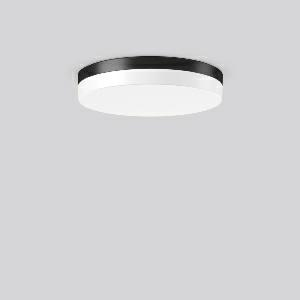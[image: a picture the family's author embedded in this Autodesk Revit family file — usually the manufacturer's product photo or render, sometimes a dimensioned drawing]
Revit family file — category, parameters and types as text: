
# Revit family: flat_slim_round_312632_0031_76_b1a7
name_source: partatom
category: Lighting Fixtures
units: mm (PartAtom-declared; Revit-internal decimal feet)

## family parameters
Cut with Voids When Loaded = No
Host = Face
Light Source = No
Part Type = Normal
Room Calculation Point = No
Round Connector Dimension = Use Diameter
Shared = No

## types (1)
- MultiLumen 1 830 (1 x LED Modul 830, 2400 lm, 3000)
    Apparent Load = 20 VA
    CIE Flux Codes = 39 70 90 83 100
    Color Rendering = 80
    Color Temperature = 3000
    Default Elevation = 1800 mm
    Height = 70 mm
    Lamp = 1 x LED Modul 830
    Lamp Light Flux = 2400 lm
    Lamp count = 1
    Length = 400 mm
    Lifetime = 50000 h
    Luminous efficacy = 120 lm/W
    Manufacturer = RZB
    ModVariant = No
    Model = 312632.0031.76
    Mounting Place = Ceiling
    Mounting Type = Surface mounted
    Number of Poles = 1
    OnlyDefault = Yes
    Power Factor = 1
    Product Name = FLAT SLIM round
    Product group = Surface mounted ceiling and wall luminaires
    ProductGroupID = 305
    Protection Class = Protection class I
    Protection Degree = Degree of protection
    RLX_Detail_Level = 1
    RLX_Emergency_Light_Flux = 0 lm
    RLX_Emergency_Type = 0
    RLX_Emergency_Type_DB = No
    RlxData = <blob elided: 21237 chars, md5=22af3205>
    Socket = socket
    Standby Power = 0 W
    System Light Flux = 2400 lm
    System Power = 20 W
    Type Comments = MultiLumen 1 830
    Type Image = 312631.0031.jpg
    URL = http://relux.com
    VarID = multilumen_1_830
    Voltage = 0 V
    Weight = 0.00 kg
    Width = 0 mm  [stored 0 ft]

note: [stored X ft] marks values corroborated as IEEE doubles in the binary element streams (Revit-internal decimal feet)

## geometry (parser evidence)
native form markers: Blend x4, Sweep x14
no freeform markers — native parametric forms only
